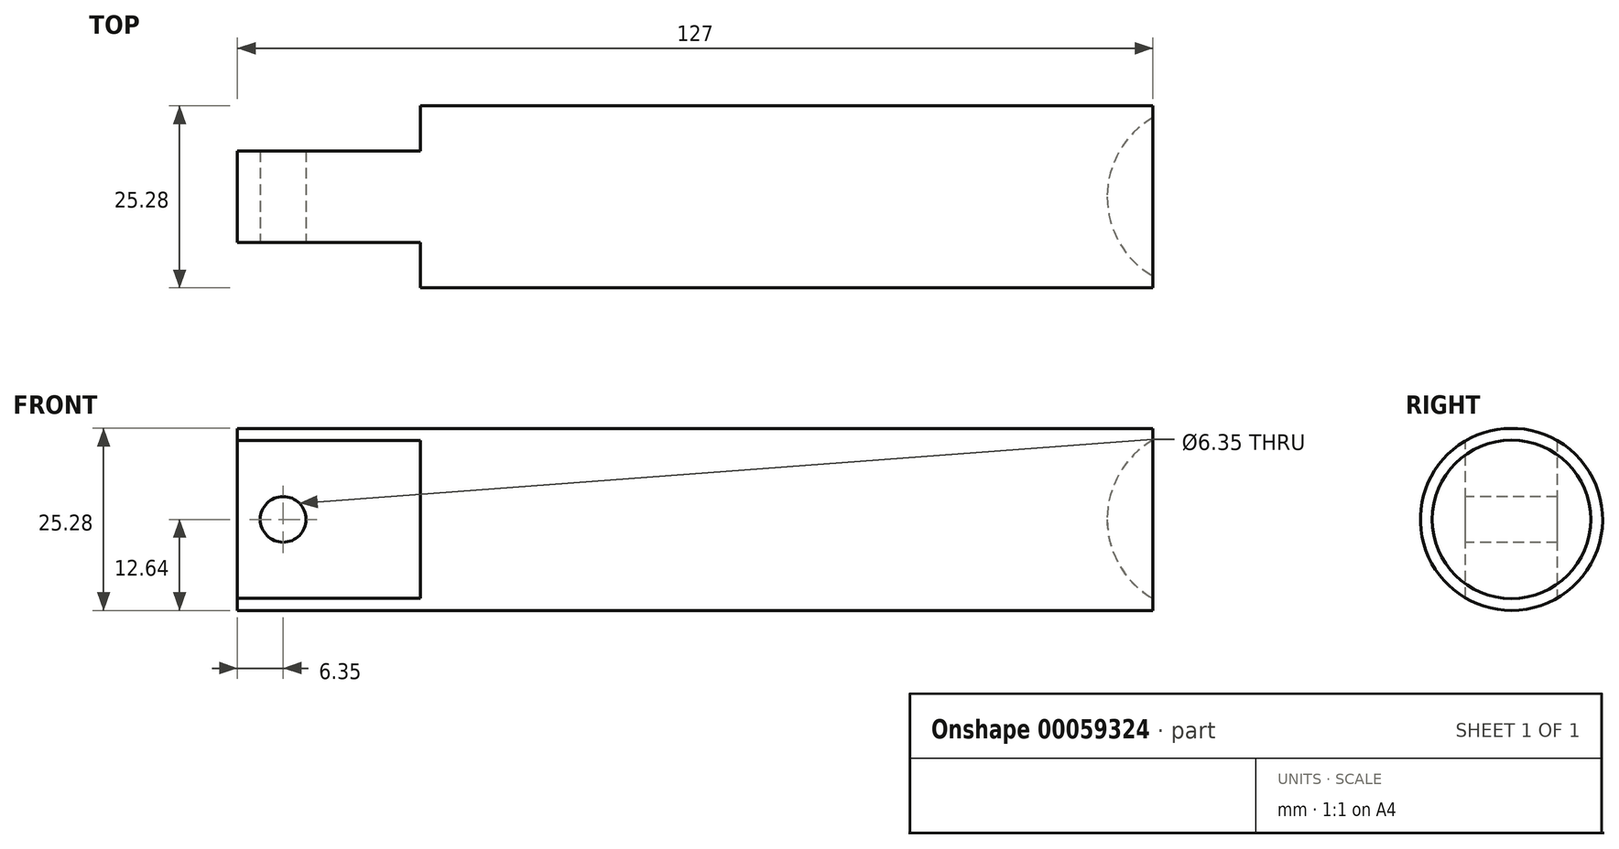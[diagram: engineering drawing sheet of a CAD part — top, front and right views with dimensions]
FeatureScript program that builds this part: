
annotation { "Feature Type Name" : "Feature", "Feature Type Description" : "" }
export const myFeature = defineFeature(function(context is Context, id is Id, definition is map)
    precondition{}
    {
        {
            var Q0;
            Q0=qCreatedBy(makeId("Right.planeOp"),FACE);
            var sketch = newSketch(context, id + "F0", { "sketchPlane" : qUnion([Q0])});
            skCircle(sketch, "E0", {"center": v(0, 0) * mm, "radius": 12.64 * mm});
            skSolve(sketch);
        }
        {
            var Q0;
            Q0 = qSketchRegion(id + "F0", true);
            extrude(context, id + "F1", {"entities" : qUnion([Q0]), "depth" : 127 * mm});
        }
        {
            var Q0;
            Q0=qCreatedBy(makeId("Right.planeOp"),FACE);
            var sketch = newSketch(context, id + "F2", { "sketchPlane" : qUnion([Q0])});
            skLineSegment(sketch, "E1.bottom", {"start": v(15.94, 19.88) * mm, "end": v(6.35, 19.88) * mm});
            skLineSegment(sketch, "E1.top", {"start": v(15.94, -18.1) * mm, "end": v(6.35, -18.1) * mm});
            skLineSegment(sketch, "E1.left", {"start": v(15.94, 19.88) * mm, "end": v(15.94, -18.1) * mm});
            skLineSegment(sketch, "E1.right", {"start": v(6.35, 19.88) * mm, "end": v(6.35, -18.1) * mm});
            skLineSegment(sketch, "E2.bottom", {"start": v(-6.35, -18.63) * mm, "end": v(-13.87, -18.63) * mm});
            skLineSegment(sketch, "E2.top", {"start": v(-6.35, 19.83) * mm, "end": v(-13.87, 19.83) * mm});
            skLineSegment(sketch, "E2.left", {"start": v(-6.35, -18.63) * mm, "end": v(-6.35, 19.83) * mm});
            skLineSegment(sketch, "E2.right", {"start": v(-13.87, -18.63) * mm, "end": v(-13.87, 19.83) * mm});
            skSolve(sketch);
        }
        {
            var Q0;
            Q0 = qSketchRegion(id + "F2", true);
            extrude(context, id + "F3", {"entities" : qUnion([Q0]), "operationType" : NewBodyOperationType.REMOVE, "depth" : 25.4 * mm});
        }
        {
            var Q0;
            Q0=qCreatedBy(makeId("Front.planeOp"),FACE);
            var sketch = newSketch(context, id + "F4", { "sketchPlane" : qUnion([Q0])});
            skCircle(sketch, "E3", {"center": v(6.35, 0) * mm, "radius": 3.18 * mm});
            skSolve(sketch);
        }
        {
            var Q0;
            Q0 = qSketchRegion(id + "F4", true);
            extrude(context, id + "F5", {"entities" : qUnion([Q0]), "operationType" : NewBodyOperationType.REMOVE, "endBound" : BoundingType.SYMMETRIC, "oppositeDirection" : true, "depth" : 25.4 * mm});
        }
        {
            var Q0;
            Q0=qCreatedBy(makeId("Front.planeOp"),FACE);
            var sketch = newSketch(context, id + "F6", { "sketchPlane" : qUnion([Q0])});
            skArc(sketch, "E4", {"start": v(146.05, 0) * mm, "mid": v(133.35, 12.7) * mm, "end": v(120.65, 0) * mm});
            skLineSegment(sketch, "E5", {"start": v(120.65, 0) * mm, "end": v(146.05, 0) * mm});
            skSolve(sketch);
        }
        {
            var Q0;
            Q0 = qSketchRegion(id + "F6", true);
            var Q1;
            Q1=sQuery(id+"F6.wireOp",EDGE,"E5");
            revolve(context, id + "F7", {"operationType" : NewBodyOperationType.REMOVE, "entities" : qUnion([Q0]), "axis" : qUnion([Q1]), "revolveType" : RevolveType.FULL, "oppositeDirection" : true});
        }
    });
